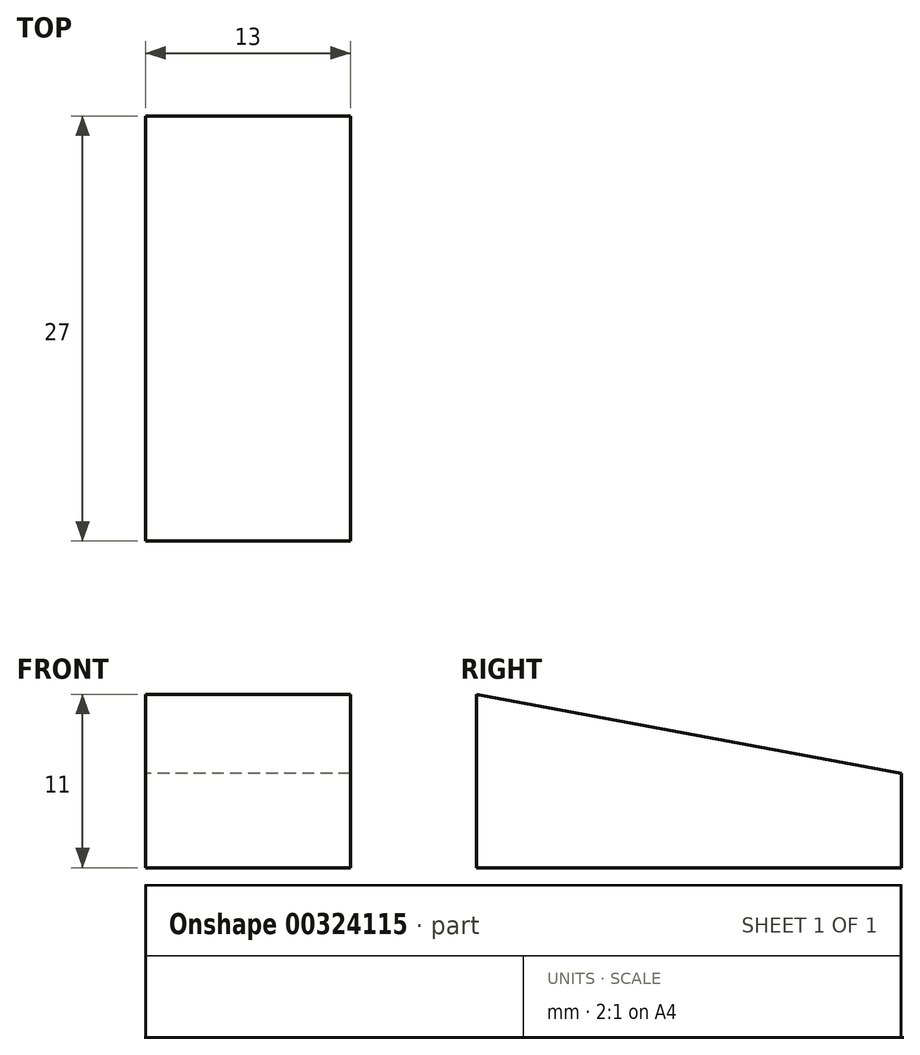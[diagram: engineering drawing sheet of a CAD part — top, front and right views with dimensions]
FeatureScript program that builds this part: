
annotation { "Feature Type Name" : "Feature", "Feature Type Description" : "" }
export const myFeature = defineFeature(function(context is Context, id is Id, definition is map)
    precondition{}
    {
        {
            var Q0;
            Q0=qCreatedBy(makeId("Right.planeOp"),FACE);
            var sketch = newSketch(context, id + "F0", { "sketchPlane" : qUnion([Q0])});
            skLineSegment(sketch, "E0", {"start": v(0, 0) * mm, "end": v(27, 0) * mm});
            skLineSegment(sketch, "E1", {"start": v(0, 0) * mm, "end": v(0, 11) * mm});
            skLineSegment(sketch, "E2", {"start": v(27, 0) * mm, "end": v(27, 6) * mm});
            skLineSegment(sketch, "E3", {"start": v(0, 11) * mm, "end": v(27, 6) * mm});
            skSolve(sketch);
        }
        {
            var Q0;
            Q0 = qSketchRegion(id + "F0", true);
            extrude(context, id + "F1", {"entities" : qUnion([Q0]), "depth" : 13 * mm});
        }
        {
            var Q0;
            Q0=qCreatedBy(makeId("Front.planeOp"),FACE);
            cPlane(context, id + "F2", {"entities" : qUnion([Q0]), "cplaneType" : CPlaneType.OFFSET, "offset" : 18 * mm, "oppositeDirection" : true, "width" : 150 * mm, "height" : 150 * mm});
        }
    });
